# Revit family: ASL_Designline_64_Al&Timber_Door_Jamb
name_source: partatom
category: Detail Items
revit_build: Autodesk Revit 2018 (Build: 20170223_1515(x64)
units: mm (PartAtom-declared; Revit-internal decimal feet)

## family parameters
Rotate with component = No
Section Shape = Not Defined
Shared = Yes

## types (6) — shared parameters
13mm Plasterboard = Yes
ASL 408 = Yes
Manufacturer = Aluminate Solutions Limited
Technical Info = www.aluminate.nz

## per-type parameters (varying)
| type | 40mm Door Jamb Standard | 50mm Door Jamb Standard | ASL Hinge Stile Hinge Door 100mm | ASL Hinge Stile Hinge Door 125mm | ASL Hinge Stile Hinge Door 75mm | Door_40 | Door_50 | Glazing | Hinge_Single | Type Comments |
| ASL 408 Single Action ASL Hinge Stile Door Suite 75mm | No | Yes | No | No | Yes | No | No | No | Yes | ASL Designline ASL 408 Jamb with Single Action ASL 75mm Hinge Stile Door Suite |
| ASL 408 Glazing | No | No | No | No | No | No | No | Yes | No | ASL Designline ASL 408 Jamb With Glazing |
| ASL 408 Single Action ASL Hinge Stile Door Suite 100mm | No | Yes | Yes | No | No | No | No | No | Yes | ASL Designline ASL 408 Jamb with Single Action PSL 100mm Hinge Stile Door Suite |
| ASL 408 Single Action ASL Hinge Stile Door Suite 125mm | No | Yes | No | Yes | No | No | No | No | Yes | ASL Designline ASL 408 Jamb with Single Action ASL 125mm Hinge Stile Door Suite |
| ASL 408 Single Action Door 40mm | Yes | No | No | No | No | Yes | No | No | No | ASL Designline ASL 408 Jamb With Single Action 40mm Timber Door |
| ASL 408 Single Action Door 50mm | No | Yes | No | No | No | No | Yes | No | Yes | ASL Designline ASL 408 Jamb With Single Action 50mm Timber Door |

## geometry (parser evidence)
native form markers: Sweep x12
no freeform markers — native parametric forms only
